# Revit family: Haworth_CabanaLounge_Table_Wedge_AP_PRELIMINARY
name_source: partatom
category: Furniture
revit_build: Autodesk Revit 2018 (Build: 20170223_1515(x64)
units: mm (PartAtom-declared; Revit-internal decimal feet)

## family parameters
Always vertical = Yes
Cut with Voids When Loaded = No
OmniClass Number = 23.40.70.14.64.21
OmniClass Title = Systems Furniture
Room Calculation Point = No
Shared = No
Work Plane-Based = No

## types (6) — shared parameters
Actual Depth = 813 mm
Actual Width = 762 mm
Assembly Code = E2020200
Description = Haworth - Cabana Lounge - Table - Wedge
Manufacturer = Haworth
Model = SECBW
Revision Number = 1
Screen Width = 762 mm
Size = Verify Final Dim. w/ Haworth
Table Depth = 813 mm
Table Width = 711 mm  [stored 2.33268 ft]
URL = https://www.haworth.com
URL - Product = https://www.haworth.com
Warranty = http://www.haworth.com

## per-type parameters (varying)
| type | Actual Height | High Screen | Low Screen | No Screen | Screen Control | Table Height | With Screen | With Top |
| Wedge Tiered - High Screen | 1372 mm  [stored 4.50131 ft] | Yes | No | No | 51 mm | 399 mm  [stored 1.30906 ft] | Yes | Yes |
| Wedge Tiered - Low Screen | 1067 mm  [stored 3.50066 ft] | No | Yes | No | 51 mm | 399 mm  [stored 1.30906 ft] | Yes | Yes |
| Wedge Tiered - No Screen | 399 mm  [stored 1.30906 ft] | No | No | Yes | 0 mm  [stored 0 ft] | 399 mm  [stored 1.30906 ft] | No | Yes |
| Wedge - No Screen | 287 mm  [stored 0.941601 ft] | No | No | Yes | 0 mm  [stored 0 ft] | 287 mm  [stored 0.941601 ft] | No | No |
| Wedge - Low Screen | 1067 mm  [stored 3.50066 ft] | No | Yes | No | 51 mm | 287 mm  [stored 0.941601 ft] | Yes | No |
| Wedge - High Screen | 1372 mm  [stored 4.50131 ft] | Yes | No | No | 51 mm | 287 mm  [stored 0.941601 ft] | Yes | No |

note: [stored X ft] marks values corroborated as IEEE doubles in the binary element streams (Revit-internal decimal feet)

## geometry (parser evidence)
native form markers: Sweep x13
no freeform markers — native parametric forms only
